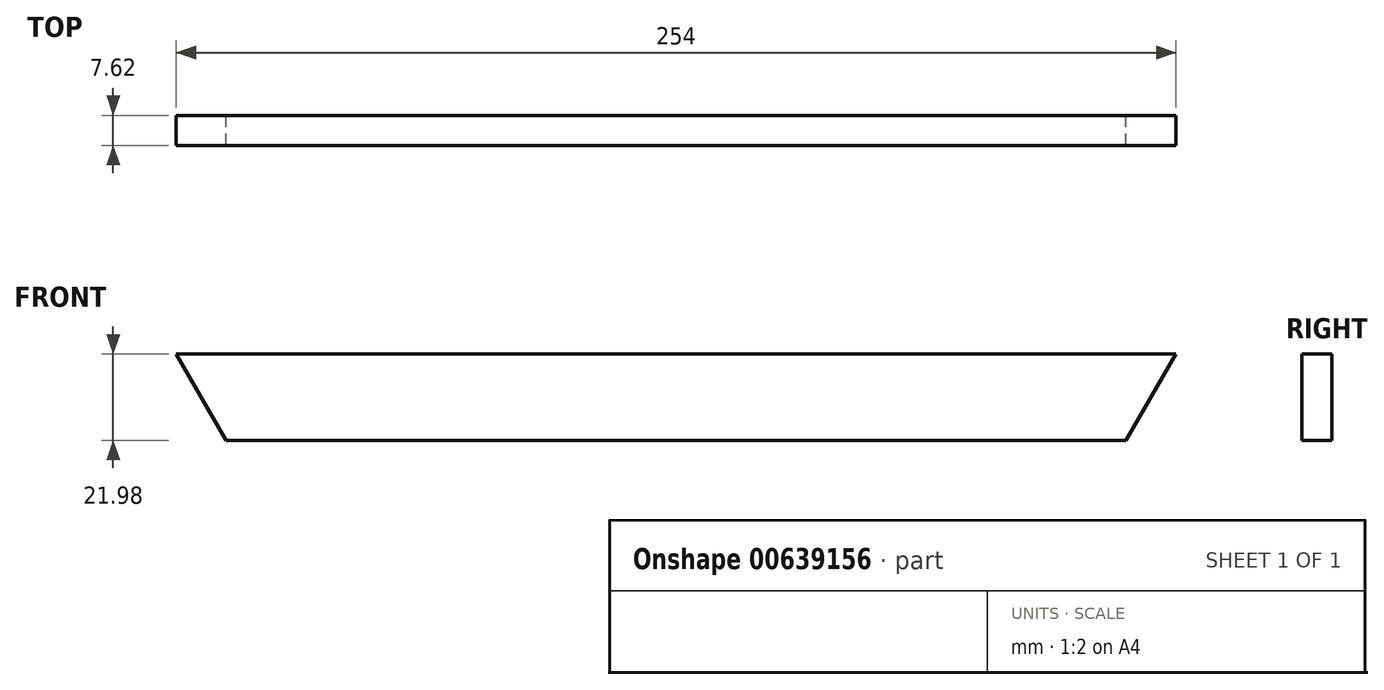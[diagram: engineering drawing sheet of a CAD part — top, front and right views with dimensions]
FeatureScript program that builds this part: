
annotation { "Feature Type Name" : "Feature", "Feature Type Description" : "" }
export const myFeature = defineFeature(function(context is Context, id is Id, definition is map)
    precondition{}
    {
        {
            var Q0;
            Q0=qCreatedBy(makeId("Front.planeOp"),FACE);
            var sketch = newSketch(context, id + "F0", { "sketchPlane" : qUnion([Q0])});
            skLineSegment(sketch, "E0", {"start": v(-125.58, 35.6) * mm, "end": v(128.42, 35.6) * mm});
            skLineSegment(sketch, "E1", {"start": v(128.42, 35.6) * mm, "end": v(115.73, 13.6) * mm});
            skLineSegment(sketch, "E2", {"start": v(115.73, 13.6) * mm, "end": v(-112.89, 13.6) * mm});
            skLineSegment(sketch, "E3", {"start": v(-112.89, 13.6) * mm, "end": v(-125.58, 35.6) * mm});
            skLineSegment(sketch, "E4", {"start": v(-112.89, 35.6) * mm, "end": v(0, 100.77) * mm});
            skLineSegment(sketch, "E5", {"start": v(0, 100.77) * mm, "end": v(115.73, 35.6) * mm});
            skLineSegment(sketch, "E6", {"start": v(0, 100.77) * mm, "end": v(0, 75.37) * mm});
            skLineSegment(sketch, "E7", {"start": v(-39, 52.85) * mm, "end": v(0, 75.37) * mm});
            skLineSegment(sketch, "E8", {"start": v(-39, 52.85) * mm, "end": v(-68.9, 35.6) * mm});
            skLineSegment(sketch, "E9", {"start": v(-112.89, 35.6) * mm, "end": v(-68.9, 35.6) * mm});
            skSolve(sketch);
        }
        {
            var Q0;
            Q0=makeQuery(id+"F0.imprint","IMPRINT",FACE,{"disambiguationData":[TD([[makeQuery(id+"F0.imprint","IMPRINT",EDGE,{"derivedFrom":sQuery(id+"F0.wireOp",EDGE,"E0")}),-1.0]])]});
            extrude(context, id + "F1", {"entities" : qUnion([Q0]), "depth" : 7.62 * mm, "offsetDistance" : 25.4 * mm});
        }
    });
